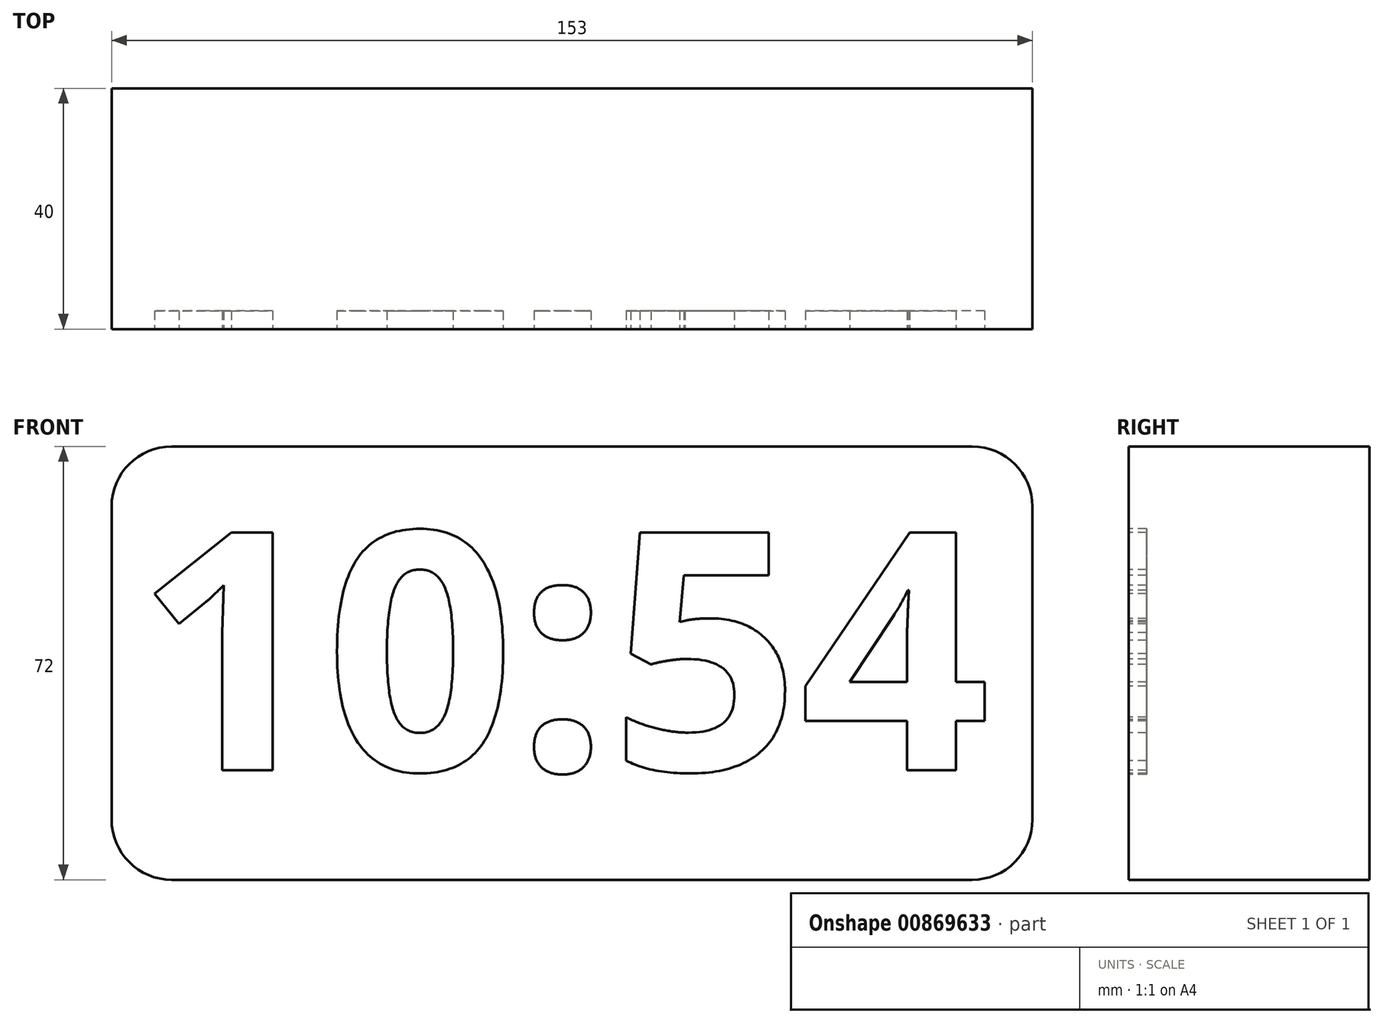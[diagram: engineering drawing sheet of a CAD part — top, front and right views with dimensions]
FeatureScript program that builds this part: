
annotation { "Feature Type Name" : "Feature", "Feature Type Description" : "" }
export const myFeature = defineFeature(function(context is Context, id is Id, definition is map)
    precondition{}
    {
        {
            var Q0;
            Q0=qCreatedBy(makeId("Front.planeOp"),FACE);
            var sketch = newSketch(context, id + "F0", { "sketchPlane" : qUnion([Q0])});
            skLineSegment(sketch, "E0.bottom", {"start": v(66.5, -36) * mm, "end": v(-66.5, -36) * mm});
            skLineSegment(sketch, "E0.top", {"start": v(66.5, 36) * mm, "end": v(-66.5, 36) * mm});
            skLineSegment(sketch, "E0.left", {"start": v(76.5, -26) * mm, "end": v(76.5, 26) * mm});
            skLineSegment(sketch, "E0.right", {"start": v(-76.5, -26) * mm, "end": v(-76.5, 26) * mm});
            skPoint(sketch, "E0.middle", {"position": v(0, 0) * mm});
            skPoint(sketch, "E1.visualSharp", {"position": v(-76.5, 36) * mm});
            skArc(sketch, "E1.filletArc", {"start": v(-66.5, 36) * mm, "mid": v(-73.57, 33.07) * mm, "end": v(-76.5, 26) * mm});
            skPoint(sketch, "E2.visualSharp", {"position": v(-76.5, -36) * mm});
            skArc(sketch, "E2.filletArc", {"start": v(-76.5, -26) * mm, "mid": v(-73.57, -33.07) * mm, "end": v(-66.5, -36) * mm});
            skPoint(sketch, "E3.visualSharp", {"position": v(76.5, -36) * mm});
            skArc(sketch, "E3.filletArc", {"start": v(66.5, -36) * mm, "mid": v(73.57, -33.07) * mm, "end": v(76.5, -26) * mm});
            skPoint(sketch, "E4.visualSharp", {"position": v(76.5, 36) * mm});
            skArc(sketch, "E4.filletArc", {"start": v(76.5, 26) * mm, "mid": v(73.57, 33.07) * mm, "end": v(66.5, 36) * mm});
            skSolve(sketch);
        }
        {
            var Q0;
            Q0=makeQuery(id+"F0.imprint","IMPRINT",FACE,{"disambiguationData":[TD([[makeQuery(id+"F0.imprint","IMPRINT",EDGE,{"derivedFrom":sQuery(id+"F0.wireOp",EDGE,"E0.bottom")}),-1.0]])]});
            extrude(context, id + "F1", {"entities" : qUnion([Q0]), "depth" : 40 * mm, "offsetDistance" : 25 * mm});
        }
        {
            var Q0;
            Q0=makeQuery(id+"F1.opExtrude","CAP_FACE",FACE,{"disambiguationData":[OSD([sQuery(id+"F0.wireOp",EDGE,"E0.bottom"),sQuery(id+"F0.wireOp",EDGE,"E0.top"),sQuery(id+"F0.wireOp",EDGE,"E0.left"),sQuery(id+"F0.wireOp",EDGE,"E0.right"),sQuery(id+"F0.wireOp",EDGE,"E1.filletArc"),sQuery(id+"F0.wireOp",EDGE,"E2.filletArc"),sQuery(id+"F0.wireOp",EDGE,"E3.filletArc"),sQuery(id+"F0.wireOp",EDGE,"E4.filletArc")])],"isStart":false});
            var sketch = newSketch(context, id + "F2", { "sketchPlane" : qUnion([Q0])});
            skText(sketch, "E5", { "text": "10:54", "fontName": "OpenSans-Bold.ttf"});
            const initialGuessF2  = {"E5": [-0.0726, -0.01779, 1, 0, 0.03982]};
            skSetInitialGuess(sketch, initialGuessF2);
            skSolve(sketch);
        }
        {
            var Q0;
            Q0 = qSketchRegion(id + "F2", true);
            extrude(context, id + "F3", {"entities" : qUnion([Q0]), "operationType" : NewBodyOperationType.REMOVE, "oppositeDirection" : true, "depth" : 3 * mm, "offsetDistance" : 25 * mm});
        }
    });
